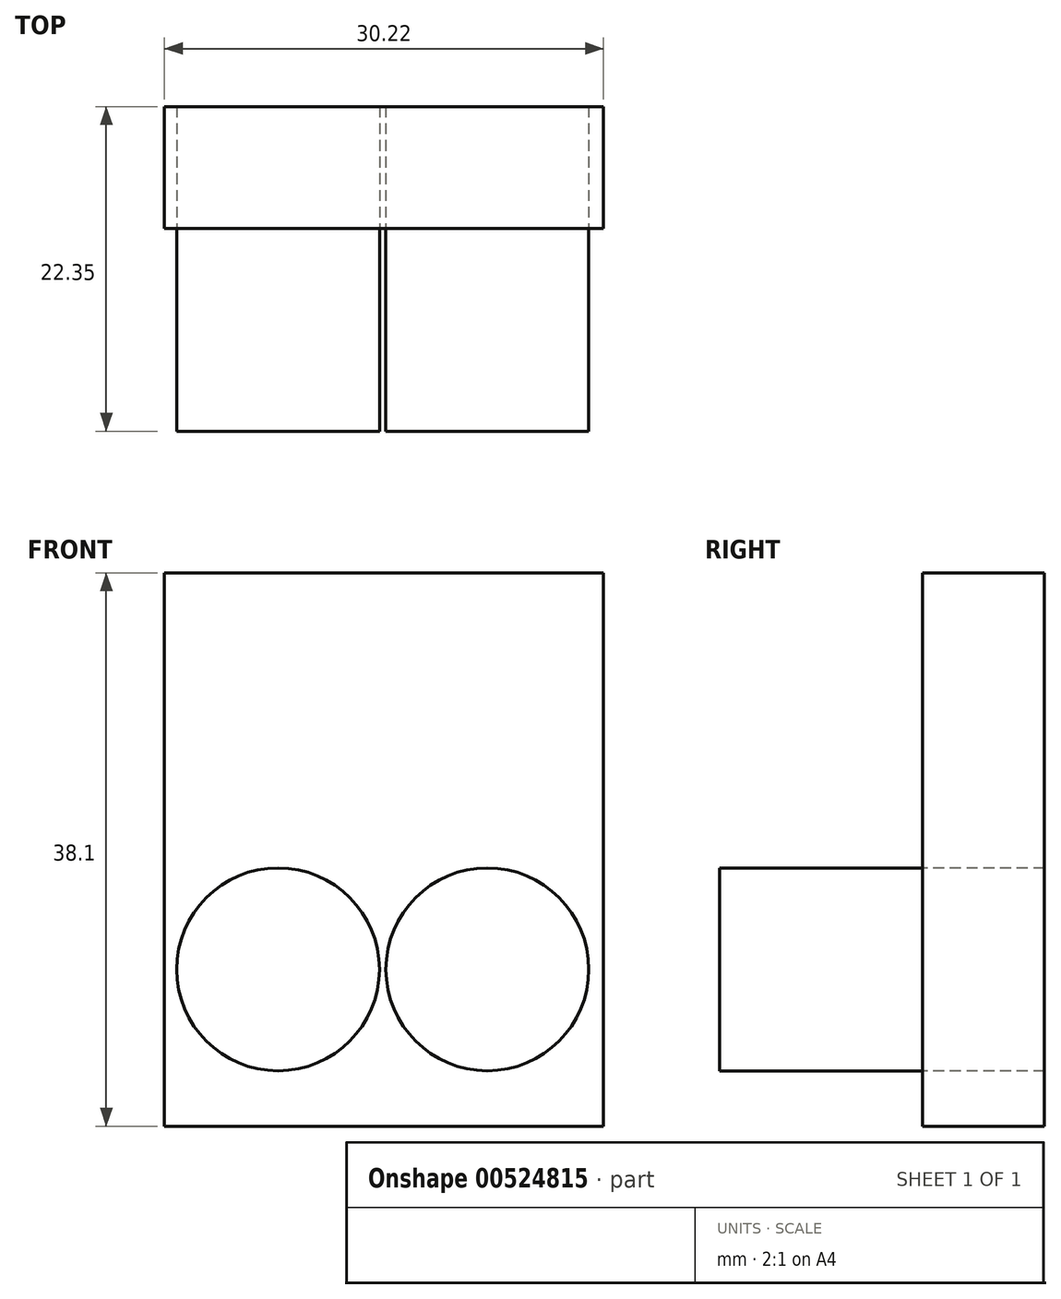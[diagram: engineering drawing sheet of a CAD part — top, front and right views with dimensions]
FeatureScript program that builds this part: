
annotation { "Feature Type Name" : "Feature", "Feature Type Description" : "" }
export const myFeature = defineFeature(function(context is Context, id is Id, definition is map)
    precondition{}
    {
        {
            var Q0;
            Q0=qCreatedBy(makeId("Front.planeOp"),FACE);
            var sketch = newSketch(context, id + "F0", { "sketchPlane" : qUnion([Q0])});
            skLineSegment(sketch, "E0.bottom", {"start": v(15.11, -19.05) * mm, "end": v(-15.11, -19.05) * mm});
            skLineSegment(sketch, "E0.top", {"start": v(15.11, 19.05) * mm, "end": v(-15.11, 19.05) * mm});
            skLineSegment(sketch, "E0.left", {"start": v(15.11, -19.05) * mm, "end": v(15.11, 19.05) * mm});
            skLineSegment(sketch, "E0.right", {"start": v(-15.11, -19.05) * mm, "end": v(-15.11, 19.05) * mm});
            skPoint(sketch, "E0.middle", {"position": v(0, 0) * mm});
            skCircle(sketch, "E1", {"center": v(7.12, -8.25) * mm, "radius": 6.99 * mm});
            skCircle(sketch, "E2", {"center": v(-7.3, -8.25) * mm, "radius": 6.99 * mm});
            skLineSegment(sketch, "E3.bottom", {"start": v(-14.6, 19.05) * mm, "end": v(14.6, 19.05) * mm});
            skLineSegment(sketch, "E3.top", {"start": v(-14.6, -19.05) * mm, "end": v(14.6, -19.05) * mm});
            skLineSegment(sketch, "E3.left", {"start": v(-14.6, 19.05) * mm, "end": v(-14.6, -19.05) * mm});
            skLineSegment(sketch, "E3.right", {"start": v(14.6, 19.05) * mm, "end": v(14.6, -19.05) * mm});
            skSolve(sketch);
        }
        {
            var Q0;
            Q0=makeQuery(id+"F0.imprint","IMPRINT",FACE,{"disambiguationData":[TD([[makeQuery(id+"F0.imprint","IMPRINT",EDGE,{"derivedFrom":sQuery(id+"F0.wireOp",EDGE,"E1")}),1.0]])]});
            var Q1;
            Q1=makeQuery(id+"F0.imprint","IMPRINT",FACE,{"disambiguationData":[TD([[makeQuery(id+"F0.imprint","IMPRINT",EDGE,{"derivedFrom":sQuery(id+"F0.wireOp",EDGE,"E2")}),1.0]])]});
            extrude(context, id + "F1", {"entities" : qUnion([Q0, Q1]), "depth" : 13.97 * mm, "offsetDistance" : 25.4 * mm});
        }
        {
            var Q0;
            Q0 = qSketchRegion(id + "F0", true);
            extrude(context, id + "F2", {"entities" : qUnion([Q0]), "oppositeDirection" : true, "depth" : 3.8 * mm, "offsetDistance" : 25.4 * mm});
        }
        {
            var Q0;
            Q0 = qSketchRegion(id + "F0", true);
            extrude(context, id + "F3", {"entities" : qUnion([Q0]), "operationType" : NewBodyOperationType.ADD, "oppositeDirection" : true, "depth" : 8.38 * mm, "offsetDistance" : 25.4 * mm});
        }
    });
